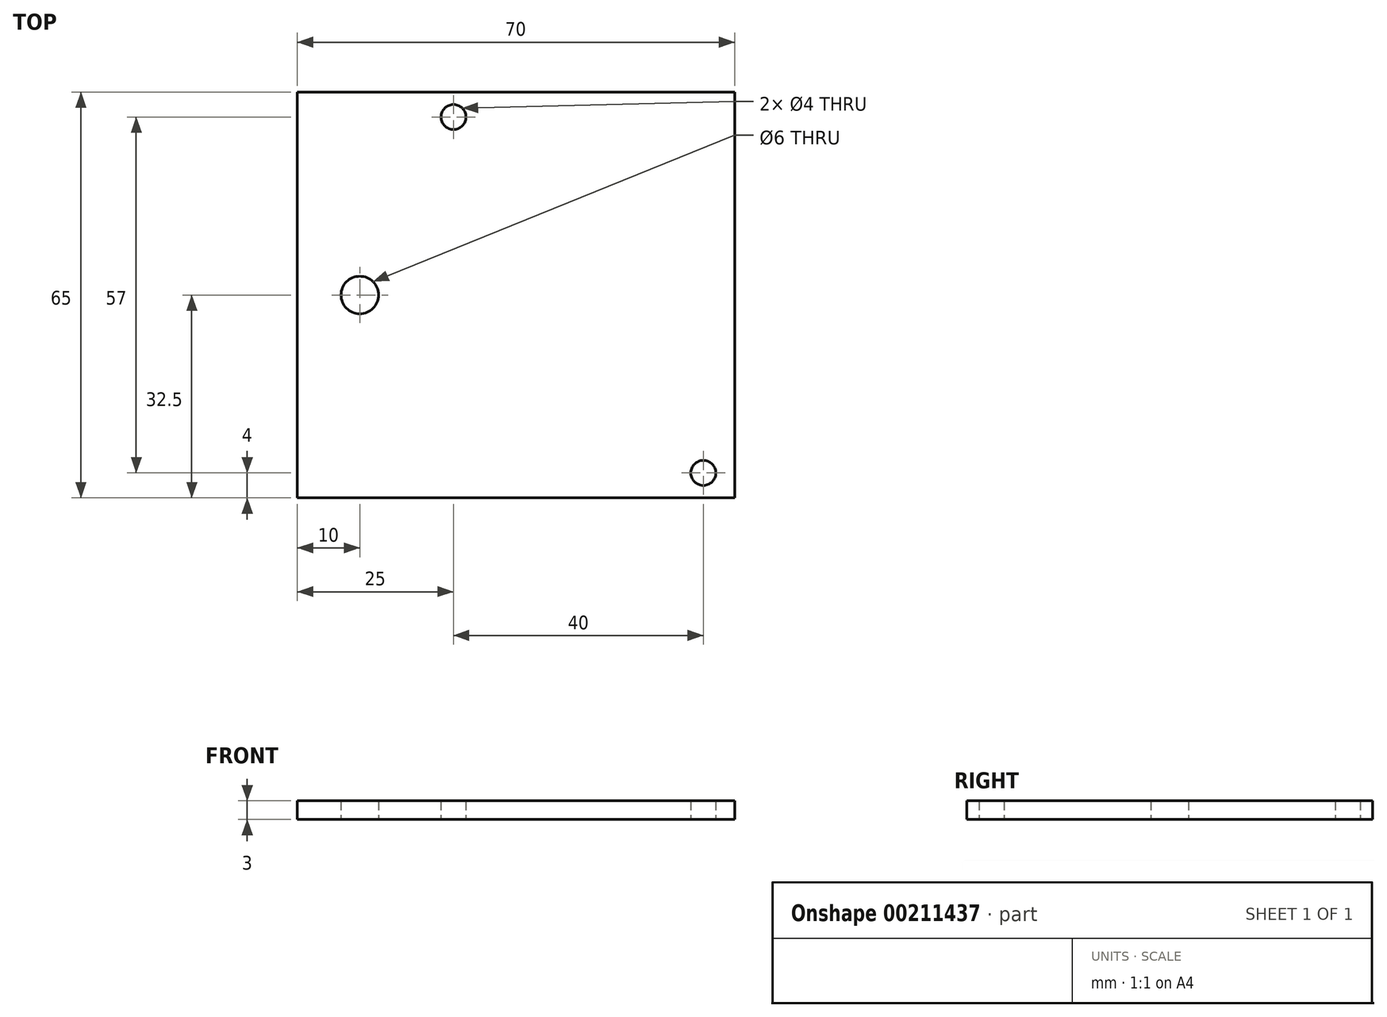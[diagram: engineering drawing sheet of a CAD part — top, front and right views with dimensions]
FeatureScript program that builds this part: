
annotation { "Feature Type Name" : "Feature", "Feature Type Description" : "" }
export const myFeature = defineFeature(function(context is Context, id is Id, definition is map)
    precondition{}
    {
        {
            var Q0;
            Q0=qCreatedBy(makeId("Top.planeOp"),FACE);
            var sketch = newSketch(context, id + "F0", { "sketchPlane" : qUnion([Q0])});
            skLineSegment(sketch, "E0.bottom", {"start": v(35, -32.5) * mm, "end": v(-35, -32.5) * mm});
            skLineSegment(sketch, "E0.top", {"start": v(35, 32.5) * mm, "end": v(-35, 32.5) * mm});
            skLineSegment(sketch, "E0.left", {"start": v(35, -32.5) * mm, "end": v(35, 32.5) * mm});
            skLineSegment(sketch, "E0.right", {"start": v(-35, -32.5) * mm, "end": v(-35, 32.5) * mm});
            skPoint(sketch, "E0.middle", {"position": v(0, 0) * mm});
            skCircle(sketch, "E1", {"center": v(-25, 0) * mm, "radius": 3 * mm});
            skCircle(sketch, "E2", {"center": v(30, -28.5) * mm, "radius": 2 * mm});
            skCircle(sketch, "E3", {"center": v(-10, 28.5) * mm, "radius": 2 * mm});
            skSolve(sketch);
        }
        {
            var Q0;
            Q0=makeQuery(id+"F0.imprint","IMPRINT",FACE,{"disambiguationData":[TD([[makeQuery(id+"F0.imprint","IMPRINT",EDGE,{"derivedFrom":sQuery(id+"F0.wireOp",EDGE,"E0.bottom")}),-1.0]])]});
            extrude(context, id + "F1", {"entities" : qUnion([Q0]), "depth" : 3 * mm});
        }
    });
